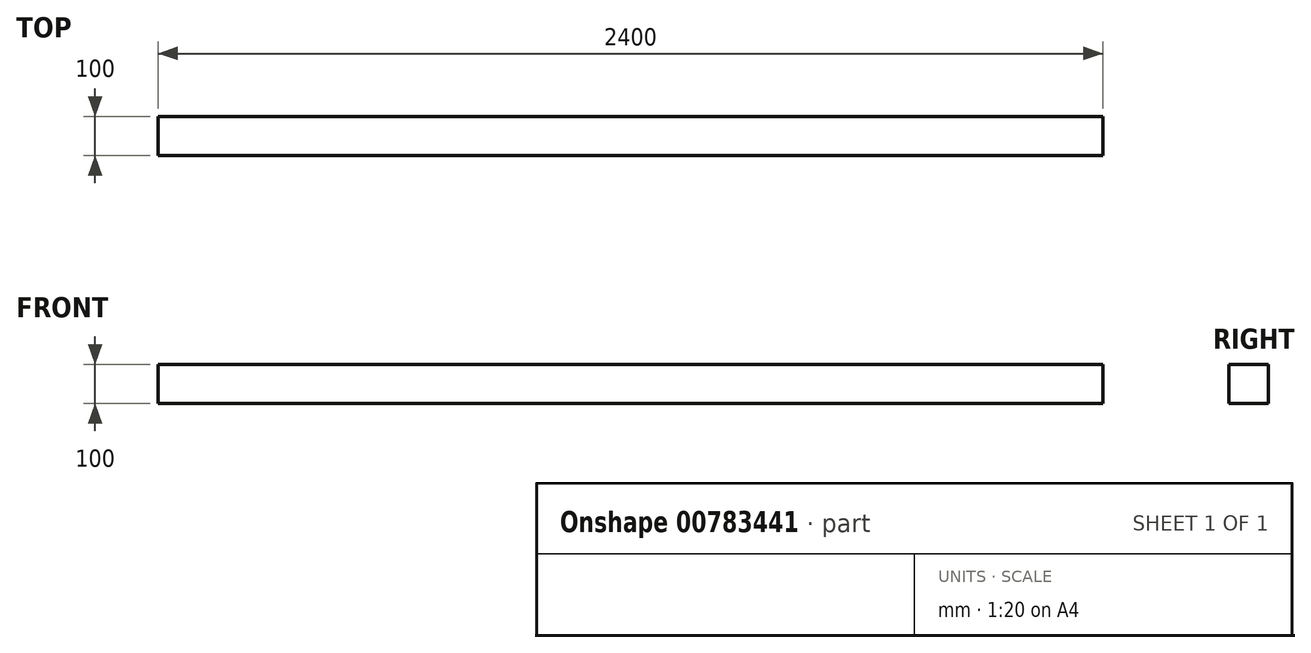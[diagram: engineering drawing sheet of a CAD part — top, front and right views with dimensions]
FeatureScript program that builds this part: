
annotation { "Feature Type Name" : "Feature", "Feature Type Description" : "" }
export const myFeature = defineFeature(function(context is Context, id is Id, definition is map)
    precondition{}
    {
        {
            var Q0;
            Q0=qCreatedBy(makeId("Front.planeOp"),FACE);
            var sketch = newSketch(context, id + "F0", { "sketchPlane" : qUnion([Q0])});
            skLineSegment(sketch, "E0.bottom", {"start": v(0, 0) * mm, "end": v(2400, 0) * mm});
            skLineSegment(sketch, "E0.top", {"start": v(0, 100) * mm, "end": v(2400, 100) * mm});
            skLineSegment(sketch, "E0.left", {"start": v(0, 0) * mm, "end": v(0, 100) * mm});
            skLineSegment(sketch, "E0.right", {"start": v(2400, 0) * mm, "end": v(2400, 100) * mm});
            skSolve(sketch);
        }
        {
            var Q0;
            Q0 = qSketchRegion(id + "F0", true);
            extrude(context, id + "F1", {"entities" : qUnion([Q0]), "depth" : 100 * mm, "offsetDistance" : 25 * mm});
        }
    });
